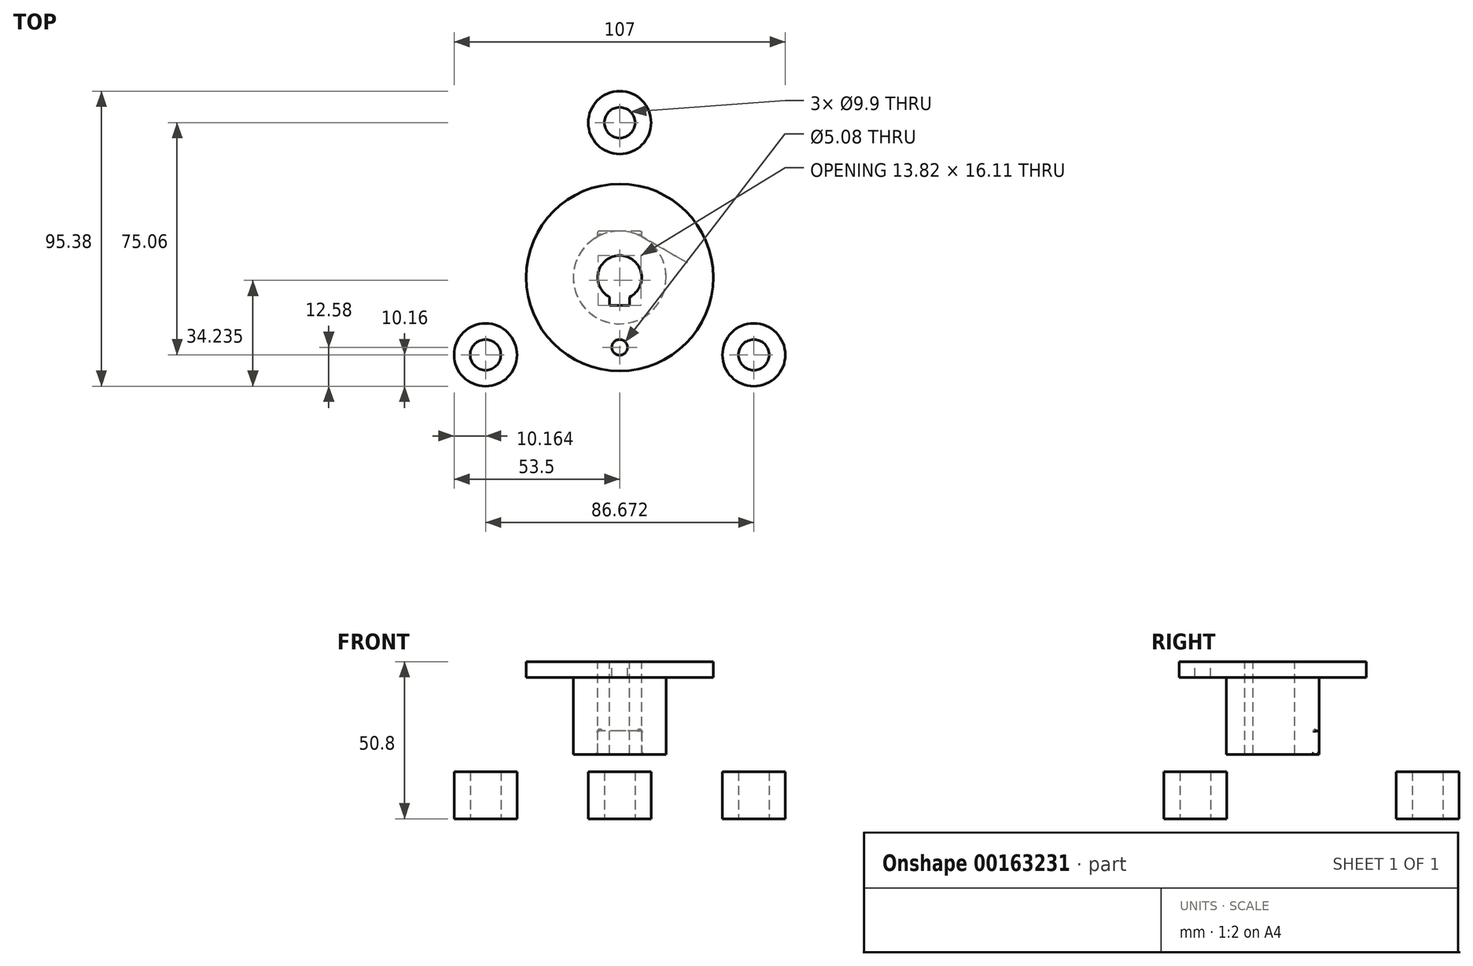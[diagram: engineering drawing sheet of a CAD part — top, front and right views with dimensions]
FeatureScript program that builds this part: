
annotation { "Feature Type Name" : "Feature", "Feature Type Description" : "" }
export const myFeature = defineFeature(function(context is Context, id is Id, definition is map)
    precondition{}
    {
        {
            var Q0;
            Q0=qCreatedBy(makeId("Top.planeOp"),FACE);
            var sketch = newSketch(context, id + "F0", { "sketchPlane" : qUnion([Q0])});
            skCircle(sketch, "E0", {"center": v(0, 0) * mm, "radius": 50.04 * mm, "construction": true});
            skCircle(sketch, "E1", {"center": v(0, 50.04) * mm, "radius": 4.95 * mm});
            skCircle(sketch, "E2", {"center": v(0, 50.04) * mm, "radius": 10.16 * mm});
            skSolve(sketch);
        }
        {
            var Q0;
            Q0=makeQuery(id+"F0.imprint","IMPRINT",FACE,{"disambiguationData":[TD([[makeQuery(id+"F0.imprint","IMPRINT",EDGE,{"derivedFrom":sQuery(id+"F0.wireOp",EDGE,"E1")}),-1.0]])]});
            var Q1;
            Q1=sQuery(id+"F0.wireOp",EDGE,"E2");
            extrude(context, id + "F1", {"entities" : qUnion([Q0]), "surfaceEntities" : qUnion([Q1]), "depth" : 15.24 * mm});
        }
        {
            var Q0;
            Q0=qCreatedBy(makeId("Top.planeOp"),FACE);
            cPlane(context, id + "F2", {"entities" : qUnion([Q0]), "cplaneType" : CPlaneType.OFFSET, "offset" : 50.8 * mm, "width" : 152.4 * mm, "height" : 152.4 * mm});
        }
        {
            var Q0;
            Q0=qCreatedBy(id+"F2.planeOp",FACE);
            var sketch = newSketch(context, id + "F3", { "sketchPlane" : qUnion([Q0])});
            skCircle(sketch, "E3", {"center": v(0, 0) * mm, "radius": 14.99 * mm});
            skCircle(sketch, "E4", {"center": v(0, 0) * mm, "radius": 30.23 * mm});
            skSolve(sketch);
        }
        {
            var Q0;
            Q0=makeQuery(id+"F3.imprint","IMPRINT",FACE,{"disambiguationData":[TD([[makeQuery(id+"F3.imprint","IMPRINT",EDGE,{"derivedFrom":sQuery(id+"F3.wireOp",EDGE,"E3")}),-1.0]])]});
            var Q1;
            Q1=makeQuery(id+"F3.imprint","IMPRINT",FACE,{"disambiguationData":[TD([[makeQuery(id+"F3.imprint","IMPRINT",EDGE,{"derivedFrom":sQuery(id+"F3.wireOp",EDGE,"E3")}),1.0]])]});
            extrude(context, id + "F4", {"entities" : qUnion([Q0, Q1]), "oppositeDirection" : true, "depth" : 5.08 * mm});
        }
        {
            var Q0;
            Q0=makeQuery(id+"F3.imprint","IMPRINT",FACE,{"disambiguationData":[TD([[makeQuery(id+"F3.imprint","IMPRINT",EDGE,{"derivedFrom":sQuery(id+"F3.wireOp",EDGE,"E3")}),1.0]])]});
            extrude(context, id + "F5", {"entities" : qUnion([Q0]), "operationType" : NewBodyOperationType.ADD, "oppositeDirection" : true, "depth" : 29.97 * mm});
        }
        {
            var Q0;
            Q0=qCreatedBy(makeId("Right.planeOp"),FACE);
            var sketch = newSketch(context, id + "F6", { "sketchPlane" : qUnion([Q0])});
            skLineSegment(sketch, "E5", {"start": v(14.99, 45.72) * mm, "end": v(14.99, 20.83) * mm});
            skLineSegment(sketch, "E6.0", {"start": v(-14.99, 20.83) * mm, "end": v(14.99, 20.83) * mm});
            skLineSegment(sketch, "E7", {"start": v(6.14, 28.45) * mm, "end": v(21.08, 28.45) * mm});
            skLineSegment(sketch, "E8", {"start": v(21.08, 28.45) * mm, "end": v(38.1, 11.43) * mm});
            skLineSegment(sketch, "E9", {"start": v(38.1, 11.43) * mm, "end": v(43.28, 11.43) * mm});
            skLineSegment(sketch, "E10.0", {"start": v(34.94, 3.81) * mm, "end": v(43.28, 3.81) * mm});
            skLineSegment(sketch, "E10.1", {"start": v(17.93, 20.83) * mm, "end": v(34.94, 3.8) * mm});
            skLineSegment(sketch, "E10.2", {"start": v(10.32, 20.83) * mm, "end": v(17.93, 20.83) * mm});
            skLineSegment(sketch, "E11", {"start": v(43.28, 3.81) * mm, "end": v(43.28, 11.43) * mm});
            skLineSegment(sketch, "E12", {"start": v(6.14, 28.45) * mm, "end": v(10.32, 20.83) * mm});
            skSolve(sketch);
        }
        {
            var Q0;
            {var subQ0=sQuery(id+"F6.wireOp",EDGE,"E7");Q0=makeQuery(id+"F6.imprint","IMPRINT",FACE,{"disambiguationData":[TD([[makeQuery(id+"F6.imprint","IMPRINT",EDGE,{"derivedFrom":subQ0}),-1.0]])]});}
            var Q1;
            {var subQ0=sQuery(id+"F6.wireOp",EDGE,"E8");Q1=makeQuery(id+"F6.imprint","IMPRINT",FACE,{"disambiguationData":[TD([[makeQuery(id+"F6.imprint","IMPRINT",EDGE,{"derivedFrom":subQ0}),-1.0]])]});}
            extrude(context, id + "F7", {"entities" : qUnion([Q0, Q1]), "operationType" : NewBodyOperationType.ADD, "depth" : 7.11 * mm, "hasSecondDirection" : true, "secondDirectionOppositeDirection" : true, "secondDirectionDepth" : 7.11 * mm});
        }
        {
            var Q0;
            Q0=makeQuery(id+"F4.opExtrude","CAP_FACE",FACE,{"disambiguationData":[OSD([sQuery(id+"F3.wireOp",EDGE,"E4")])],"isStart":true});
            var sketch = newSketch(context, id + "F8", { "sketchPlane" : qUnion([Q0])});
            skPoint(sketch, "E13", {"position": v(0, 0) * mm});
            skCircle(sketch, "E14", {"center": v(0, 0) * mm, "radius": 22.6 * mm, "construction": true});
            skPoint(sketch, "E15", {"position": v(0, -22.6) * mm});
            skSolve(sketch);
        }
        {
            var Q0;
            Q0=makeQuery(id+"F1.opExtrude","SWEPT_BODY",BODY,{"disambiguationData":[OSD([sQuery(id+"F0.wireOp",EDGE,"E1"),sQuery(id+"F0.wireOp",EDGE,"E2")])]});
            var Q1;
            Q1=makeQuery(id+"F4.opExtrude","SWEPT_FACE",FACE,{"disambiguationData":[OSD([sQuery(id+"F3.wireOp",EDGE,"E4")])]});
            circularPattern(context, id + "F9", {"entities" : qUnion([Q0]), "axis" : qUnion([Q1]), "angle" : 360 * degree, "instanceCount" : 3, "equalSpace" : true});
        }
        {
            var Q0;
            Q0=sQuery(id+"F8.wireOp",VERTEX,"E13");
            var Q1;
            Q1=makeQuery(id+"F4.opExtrude","SWEPT_BODY",BODY,{"disambiguationData":[OSD([sQuery(id+"F3.wireOp",EDGE,"E4")])]});
            var Q2;
            Q2=makeQuery(id+"F1.opExtrude","SWEPT_BODY",BODY,{"disambiguationData":[OSD([sQuery(id+"F0.wireOp",EDGE,"E1"),sQuery(id+"F0.wireOp",EDGE,"E2")])]});
            hole(context, id + "F10", {"style" : HoleStyle.SIMPLE, "endStyle" : HoleEndStyle.THROUGH, "holeDiameter" : 14.22 * mm, "locations" : qUnion([Q0]), "scope" : qUnion([Q1, Q2]), "isTappedThrough" : true});
        }
        {
            var Q0;
            Q0=sQuery(id+"F8.wireOp",VERTEX,"E15");
            var Q1;
            Q1=makeQuery(id+"F4.opExtrude","SWEPT_BODY",BODY,{"disambiguationData":[OSD([sQuery(id+"F3.wireOp",EDGE,"E4")])]});
            hole(context, id + "F11", {"style" : HoleStyle.SIMPLE, "endStyle" : HoleEndStyle.THROUGH, "holeDiameter" : 5.08 * mm, "locations" : qUnion([Q0]), "scope" : qUnion([Q1]), "isTappedThrough" : true});
        }
        {
            var Q0;
            Q0=makeQuery(id+"F8.imprint","IMPRINT",FACE,{"disambiguationData":[TD([[makeQuery(id+"F8.imprint","IMPRINT",EDGE,{"derivedFrom":makeQuery(id+"F4.opExtrude","CAP_EDGE",EDGE,{"disambiguationData":[OSD([sQuery(id+"F3.wireOp",EDGE,"E4")])],"isStart":true})}),1.0]])]});
            var sketch = newSketch(context, id + "F12", { "sketchPlane" : qUnion([Q0])});
            skLineSegment(sketch, "E16.bottom", {"start": v(3.24, -4.4) * mm, "end": v(-3.24, -4.4) * mm});
            skLineSegment(sketch, "E16.top", {"start": v(3.24, -9) * mm, "end": v(-3.24, -9) * mm});
            skLineSegment(sketch, "E16.left", {"start": v(3.24, -4.4) * mm, "end": v(3.24, -9) * mm});
            skLineSegment(sketch, "E16.right", {"start": v(-3.24, -4.4) * mm, "end": v(-3.24, -9) * mm});
            skSolve(sketch);
        }
        {
            var Q0;
            Q0 = qSketchRegion(id + "F12", true);
            extrude(context, id + "F13", {"entities" : qUnion([Q0]), "operationType" : NewBodyOperationType.REMOVE, "endBound" : BoundingType.THROUGH_ALL, "oppositeDirection" : true, "depth" : 25.4 * mm});
        }
        {
            var Q0;
            Q0=makeQuery(id+"F7.opExtrude","SWEPT_FACE",FACE,{"disambiguationData":[OSD([sQuery(id+"F6.wireOp",EDGE,"E8")])]});
            var Q1;
            Q1=makeQuery(id+"F9.opPattern","COPY",FACE,{"derivedFrom":makeQuery(id+"F7.opExtrude","SWEPT_FACE",FACE,{"disambiguationData":[OSD([sQuery(id+"F6.wireOp",EDGE,"E8")])]}),"instanceName":"1"});
            var Q2;
            Q2=makeQuery(id+"F9.opPattern","COPY",FACE,{"derivedFrom":makeQuery(id+"F7.opExtrude","CAP_FACE",FACE,{"disambiguationData":[OSD([sQuery(id+"F6.wireOp",EDGE,"E7"),sQuery(id+"F6.wireOp",EDGE,"E8"),sQuery(id+"F6.wireOp",EDGE,"E9"),sQuery(id+"F6.wireOp",EDGE,"E10.0"),sQuery(id+"F6.wireOp",EDGE,"E10.1"),sQuery(id+"F6.wireOp",EDGE,"E10.2"),sQuery(id+"F6.wireOp",EDGE,"E11"),sQuery(id+"F6.wireOp",EDGE,"E12")])],"isStart":false}),"instanceName":"1"});
            var Q3;
            Q3=makeQuery(id+"F7.opExtrude","CAP_FACE",FACE,{"disambiguationData":[OSD([sQuery(id+"F6.wireOp",EDGE,"E7"),sQuery(id+"F6.wireOp",EDGE,"E8"),sQuery(id+"F6.wireOp",EDGE,"E9"),sQuery(id+"F6.wireOp",EDGE,"E10.0"),sQuery(id+"F6.wireOp",EDGE,"E10.1"),sQuery(id+"F6.wireOp",EDGE,"E10.2"),sQuery(id+"F6.wireOp",EDGE,"E11"),sQuery(id+"F6.wireOp",EDGE,"E12")])],"isStart":true});
            var Q4;
            Q4=makeQuery(id+"F7.opExtrude","CAP_FACE",FACE,{"disambiguationData":[OSD([sQuery(id+"F6.wireOp",EDGE,"E7"),sQuery(id+"F6.wireOp",EDGE,"E8"),sQuery(id+"F6.wireOp",EDGE,"E9"),sQuery(id+"F6.wireOp",EDGE,"E10.0"),sQuery(id+"F6.wireOp",EDGE,"E10.1"),sQuery(id+"F6.wireOp",EDGE,"E10.2"),sQuery(id+"F6.wireOp",EDGE,"E11"),sQuery(id+"F6.wireOp",EDGE,"E12")])],"isStart":false});
            var Q5;
            Q5=makeQuery(id+"F9.opPattern","COPY",FACE,{"derivedFrom":makeQuery(id+"F7.opExtrude","CAP_FACE",FACE,{"disambiguationData":[OSD([sQuery(id+"F6.wireOp",EDGE,"E7"),sQuery(id+"F6.wireOp",EDGE,"E8"),sQuery(id+"F6.wireOp",EDGE,"E9"),sQuery(id+"F6.wireOp",EDGE,"E10.0"),sQuery(id+"F6.wireOp",EDGE,"E10.1"),sQuery(id+"F6.wireOp",EDGE,"E10.2"),sQuery(id+"F6.wireOp",EDGE,"E11"),sQuery(id+"F6.wireOp",EDGE,"E12")])],"isStart":true}),"instanceName":"2"});
            var Q6;
            Q6=makeQuery(id+"F9.opPattern","COPY",FACE,{"derivedFrom":makeQuery(id+"F7.opExtrude","SWEPT_FACE",FACE,{"disambiguationData":[OSD([sQuery(id+"F6.wireOp",EDGE,"E8")])]}),"instanceName":"2"});
            var Q7;
            Q7=makeQuery(id+"F9.opPattern","COPY",FACE,{"derivedFrom":makeQuery(id+"F7.opExtrude","CAP_FACE",FACE,{"disambiguationData":[OSD([sQuery(id+"F6.wireOp",EDGE,"E7"),sQuery(id+"F6.wireOp",EDGE,"E8"),sQuery(id+"F6.wireOp",EDGE,"E9"),sQuery(id+"F6.wireOp",EDGE,"E10.0"),sQuery(id+"F6.wireOp",EDGE,"E10.1"),sQuery(id+"F6.wireOp",EDGE,"E10.2"),sQuery(id+"F6.wireOp",EDGE,"E11"),sQuery(id+"F6.wireOp",EDGE,"E12")])],"isStart":false}),"instanceName":"2"});
            fillet(context, id + "F14", {"entities" : qUnion([Q0, Q1, Q2, Q3, Q4, Q5, Q6, Q7]), "radius" : 0.5 * mm, "tangentPropagation" : true, "allowEdgeOverflow" : false});
        }
    });
